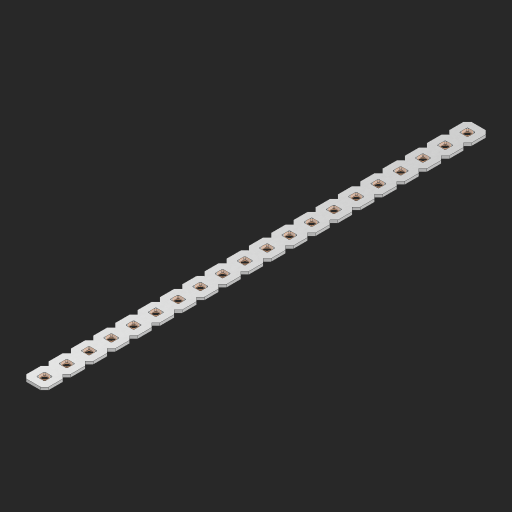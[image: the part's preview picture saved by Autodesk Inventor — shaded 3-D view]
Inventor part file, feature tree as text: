
AUTODESK INVENTOR PART (.ipt)
format: ipt  version: 2023 (Build 270158000, 158)  size: 488,448 bytes
history: native  units: in
note: dims shown in document units (in); Inventor stores cm internally (conversion verified against a paired STEP export)
features: other x21, extrude x19, sketch x2, pattern_linear x1
ambient origin geometry x8: Origin, YZ Plane, XZ Plane, XY Plane, X Axis, Y Axis, Z Axis, Center Point
bodies: Solid1 (feature_tree), Body (feature_tree)
feature tree (43):
  pattern_linear  "Rectangular Pattern1"  Spacing1=0.09in  [1 undecoded]
  sketch  "Sketch1"  dims[d1=0.5in]
  sketch  "Sketch2"  dims[d2=0.182in d3=0.09in d4=0.09in d5=0.09in d6=0.09in d7=0.09in d8=0.09in d9=0.09in d10=0.09in d11=0.02in d13=0.0in d14=0.172in d15=0.0625in d16=0.0in d19=0.5in d22=0.5in]
  other  "Srf1"
  other  "Srf126"
  other  "Srf127"
  other  "Srf128"
  other  "Srf129"
  other  "Srf130"
  other  "Srf131"
  other  "Srf250"
  other  "Srf251"
  other  "Srf252"
  other  "Srf253"
  other  "Srf254"
  other  "Srf255"
  other  "Srf256"
  other  "Srf257"
  other  "Srf258"
  other  "Srf259"
  other  "Srf260"
  other  "Srf261"
  other  "Srf262"
  other  "Circle"
  extrude  "ExtrusionSrf126"  Depth=0.09in
  extrude  "ExtrusionSrf127"  Depth=0.09in
  extrude  "ExtrusionSrf128"  Depth=0.09in
  extrude  "ExtrusionSrf129"  Depth=0.09in
  extrude  "ExtrusionSrf130"  Depth=0.09in
  extrude  "ExtrusionSrf131"  Depth=0.09in
  extrude  "ExtrusionSrf250"  Depth=0.09in
  extrude  "ExtrusionSrf251"  Depth=0.02in
  extrude  "ExtrusionSrf252"  TaperAngle=0.0deg  [1 undecoded]
  extrude  "ExtrusionSrf253"  Depth=0.5in
  extrude  "ExtrusionSrf254"  Depth=0.0625in TaperAngle=0.0deg
  extrude  "ExtrusionSrf255"  Depth=0.5in
  extrude  "ExtrusionSrf256"  Depth=0.5in
  extrude  "ExtrusionSrf257"  [1 undecoded]
  extrude  "ExtrusionSrf258"  [1 undecoded]
  extrude  "ExtrusionSrf259"  [1 undecoded]
  extrude  "ExtrusionSrf260"  [1 undecoded]
  extrude  "ExtrusionSrf261"  [1 undecoded]
  extrude  "ExtrusionSrf262"  [1 undecoded]
note: 8 required parameter values undecoded (feature->parameter linkage not recoverable at this tier; creation-order binding heuristic only, values carry confidence <= 0.55)
